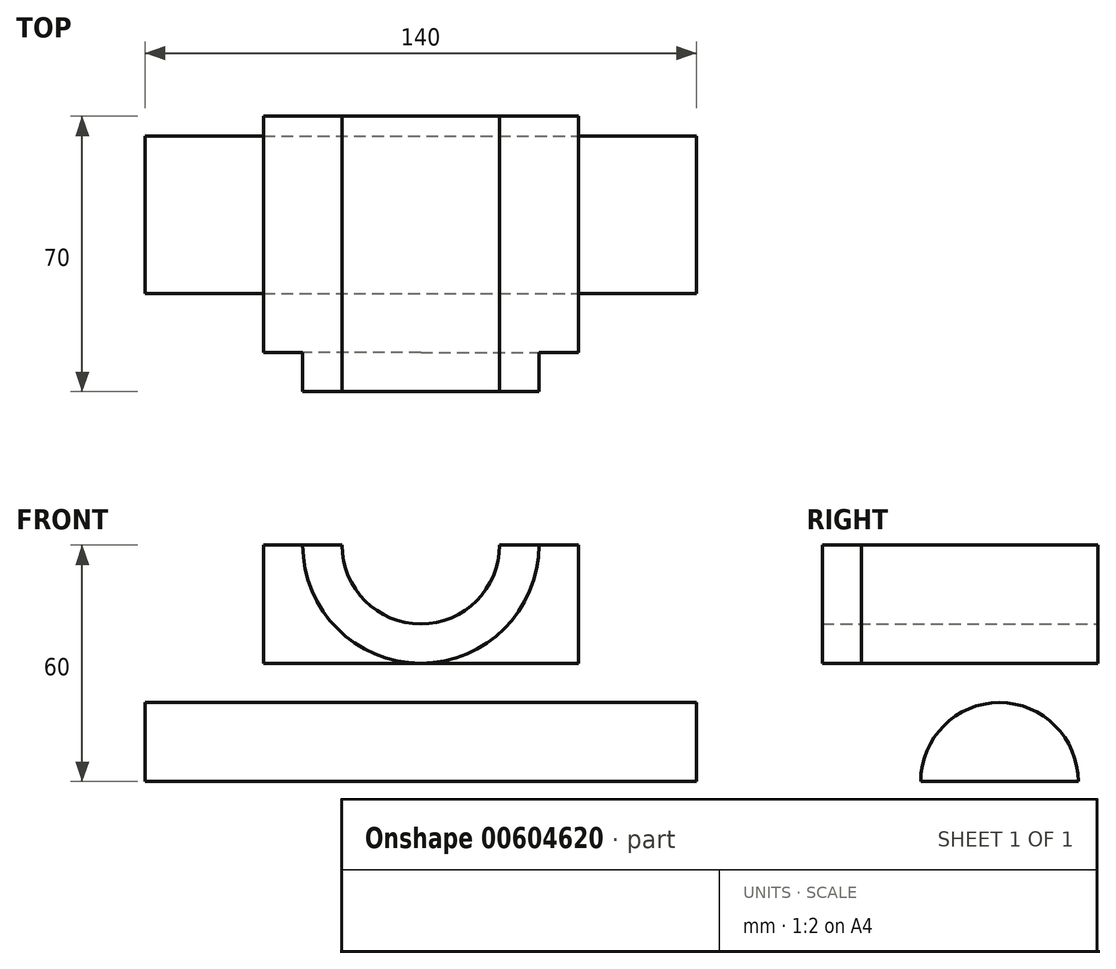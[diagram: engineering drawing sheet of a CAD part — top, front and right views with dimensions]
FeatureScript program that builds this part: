
annotation { "Feature Type Name" : "Feature", "Feature Type Description" : "" }
export const myFeature = defineFeature(function(context is Context, id is Id, definition is map)
    precondition{}
    {
        {
            var Q0;
            Q0=qCreatedBy(makeId("Front.planeOp"),FACE);
            var sketch = newSketch(context, id + "F0", { "sketchPlane" : qUnion([Q0])});
            skLineSegment(sketch, "E0.bottom", {"start": v(0, 0) * mm, "end": v(70, 0) * mm});
            skLineSegment(sketch, "E0.top", {"start": v(20, 60) * mm, "end": v(70, 60) * mm});
            skLineSegment(sketch, "E0.left", {"start": v(0, 0) * mm, "end": v(0, 40) * mm});
            skLineSegment(sketch, "E0.right", {"start": v(70, 0) * mm, "end": v(70, 60) * mm});
            skArc(sketch, "E1", {"start": v(0, 40) * mm, "mid": v(14.14, 45.86) * mm, "end": v(20, 60) * mm});
            skSolve(sketch);
        }
        {
            var Q0;
            Q0 = qSketchRegion(id + "F0", true);
            extrude(context, id + "F1", {"entities" : qUnion([Q0]), "endBound" : BoundingType.SYMMETRIC, "depth" : 70 * mm, "offsetDistance" : 25 * mm});
        }
        {
            var Q0;
            Q0=makeQuery(id+"F1.opExtrude","CAP_FACE",FACE,{"disambiguationData":[OSD([sQuery(id+"F0.wireOp",EDGE,"E0.bottom"),sQuery(id+"F0.wireOp",EDGE,"E0.top"),sQuery(id+"F0.wireOp",EDGE,"E0.left"),sQuery(id+"F0.wireOp",EDGE,"E0.right"),sQuery(id+"F0.wireOp",EDGE,"E1")])],"isStart":false});
            var sketch = newSketch(context, id + "F2", { "sketchPlane" : qUnion([Q0])});
            skLineSegment(sketch, "E2.bottom", {"start": v(70, 60) * mm, "end": v(40, 60) * mm});
            skLineSegment(sketch, "E2.top", {"start": v(70, 30) * mm, "end": v(40, 30) * mm});
            skLineSegment(sketch, "E2.left", {"start": v(70, 60) * mm, "end": v(70, 30) * mm});
            skLineSegment(sketch, "E2.right", {"start": v(40, 60) * mm, "end": v(40, 30) * mm});
            skSolve(sketch);
        }
        {
            var Q0;
            Q0=makeQuery(id+"F2.imprint","IMPRINT",FACE,{"disambiguationData":[TD([[makeQuery(id+"F2.imprint","IMPRINT",EDGE,{"derivedFrom":sQuery(id+"F2.wireOp",EDGE,"E2.bottom")}),-1.0]])]});
            extrude(context, id + "F3", {"entities" : qUnion([Q0]), "operationType" : NewBodyOperationType.REMOVE, "oppositeDirection" : true, "depth" : 60 * mm, "offsetDistance" : 25 * mm});
        }
        {
            var Q0;
            Q0=makeQuery(id+"F3.boolean.opBoolean","COPY",FACE,{"derivedFrom":makeQuery(id+"F3.opExtrude","CAP_FACE",FACE,{"disambiguationData":[OSD([sQuery(id+"F2.wireOp",EDGE,"E2.bottom"),sQuery(id+"F2.wireOp",EDGE,"E2.top"),sQuery(id+"F2.wireOp",EDGE,"E2.left"),sQuery(id+"F2.wireOp",EDGE,"E2.right")])],"isStart":false})});
            var sketch = newSketch(context, id + "F4", { "sketchPlane" : qUnion([Q0])});
            skCircle(sketch, "E3", {"center": v(55, 45) * mm, "radius": 5 * mm});
            skPoint(sketch, "E3.centerSnap0", {"position": v(70, 45) * mm});
            skPoint(sketch, "E3.centerSnap1", {"position": v(55, 60) * mm});
            skSolve(sketch);
        }
        {
            var Q0;
            Q0 = qSketchRegion(id + "F4", true);
            extrude(context, id + "F5", {"entities" : qUnion([Q0]), "operationType" : NewBodyOperationType.REMOVE, "endBound" : BoundingType.THROUGH_ALL, "oppositeDirection" : true, "depth" : 25 * mm, "offsetDistance" : 25 * mm});
        }
        {
            var Q0;
            Q0=makeQuery(id+"F1.opExtrude","SWEPT_FACE",FACE,{"disambiguationData":[OSD([sQuery(id+"F0.wireOp",EDGE,"E0.right")])]});
            var sketch = newSketch(context, id + "F6", { "sketchPlane" : qUnion([Q0])});
            skArc(sketch, "E4", {"start": v(-20, 0) * mm, "mid": v(0, 20) * mm, "end": v(20, 0) * mm});
            skSolve(sketch);
        }
        {
            var Q0;
            {var subQ0=sQuery(id+"F6.wireOp",EDGE,"E4");Q0=makeQuery(id+"F6.imprint","IMPRINT",FACE,{"disambiguationData":[TD([[makeQuery(id+"F6.imprint","IMPRINT",EDGE,{"derivedFrom":subQ0}),-1.0]])]});}
            extrude(context, id + "F7", {"entities" : qUnion([Q0]), "operationType" : NewBodyOperationType.REMOVE, "endBound" : BoundingType.THROUGH_ALL, "oppositeDirection" : true, "depth" : 25 * mm, "offsetDistance" : 25 * mm});
        }
        {
            var Q0;
            Q0=makeQuery(id+"F1.opExtrude","CAP_FACE",FACE,{"disambiguationData":[OSD([sQuery(id+"F0.wireOp",EDGE,"E0.bottom"),sQuery(id+"F0.wireOp",EDGE,"E0.top"),sQuery(id+"F0.wireOp",EDGE,"E0.left"),sQuery(id+"F0.wireOp",EDGE,"E0.right"),sQuery(id+"F0.wireOp",EDGE,"E1")])],"isStart":false});
            var sketch = newSketch(context, id + "F8", { "sketchPlane" : qUnion([Q0])});
            skArc(sketch, "E5.0", {"start": v(0, 30) * mm, "mid": v(21.21, 38.79) * mm, "end": v(30, 60) * mm});
            skArc(sketch, "E6.0", {"start": v(0, 40) * mm, "mid": v(14.14, 45.86) * mm, "end": v(20, 60) * mm});
            skSolve(sketch);
        }
        {
            var Q0;
            {var subQ0=sQuery(id+"F8.wireOp",EDGE,"E5.0");Q0=makeQuery(id+"F8.imprint","IMPRINT",FACE,{"disambiguationData":[TD([[makeQuery(id+"F8.imprint","IMPRINT",EDGE,{"derivedFrom":subQ0}),1.0]])]});}
            extrude(context, id + "F9", {"entities" : qUnion([Q0]), "operationType" : NewBodyOperationType.ADD, "depth" : 10 * mm, "offsetDistance" : 25 * mm});
        }
        {
            var Q0;
            Q0=makeQuery(id+"F1.opExtrude","SWEPT_BODY",BODY,{"disambiguationData":[OSD([sQuery(id+"F0.wireOp",EDGE,"E0.bottom"),sQuery(id+"F0.wireOp",EDGE,"E0.top"),sQuery(id+"F0.wireOp",EDGE,"E0.left"),sQuery(id+"F0.wireOp",EDGE,"E0.right"),sQuery(id+"F0.wireOp",EDGE,"E1")])]});
            var Q1;
            Q1=qCreatedBy(makeId("Right.planeOp"),FACE);
            mirror(context, id + "F10", {"operationType" : NewBodyOperationType.ADD, "entities" : qUnion([Q0]), "mirrorPlane" : qUnion([Q1])});
        }
    });
